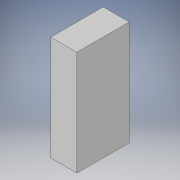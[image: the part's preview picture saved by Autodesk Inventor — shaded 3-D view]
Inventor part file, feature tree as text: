
AUTODESK INVENTOR PART (.ipt)
format: ipt  version: 2017 (Build 210142000, 142)  size: 87,552 bytes
history: native  units: in
note: dims shown in document units (in); Inventor stores cm internally (conversion verified against a paired STEP export)
features: extrude x1, sketch x1
ambient origin geometry x8: Origin, YZ Plane, XZ Plane, XY Plane, X Axis, Y Axis, Z Axis, Center Point
bodies: Solid1 (feature_tree)
feature tree (2):
  extrude  "Extrusion1"  Depth=1.5in
  sketch  "Sketch1"  dims[d0=0.75in d1=1.5in d2=3.0in d3=0.0in]
